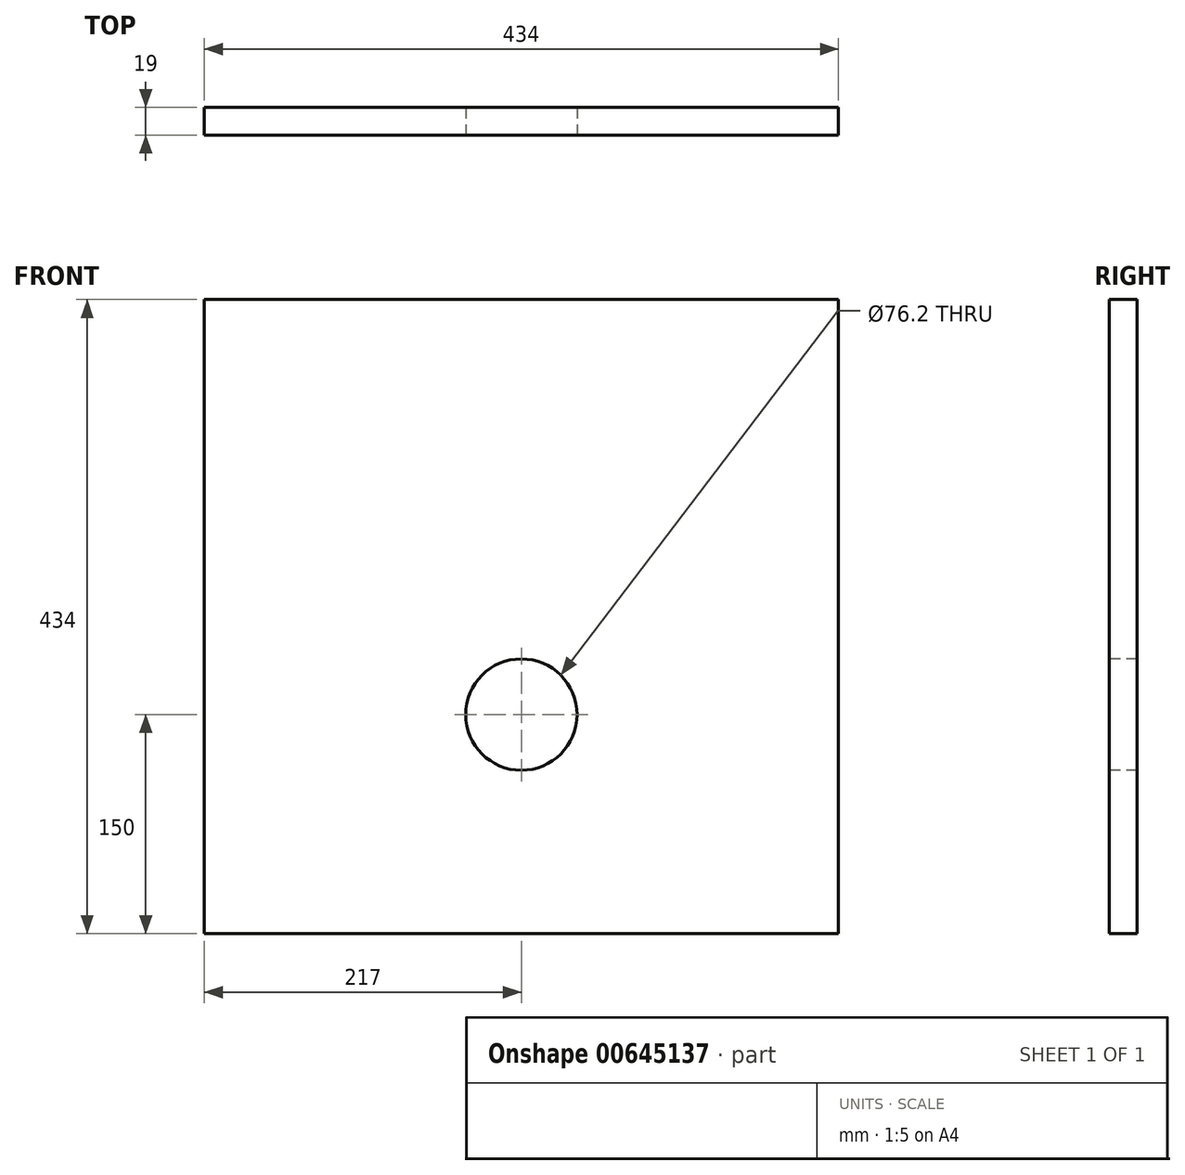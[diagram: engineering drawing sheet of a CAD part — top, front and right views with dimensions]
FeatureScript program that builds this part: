
annotation { "Feature Type Name" : "Feature", "Feature Type Description" : "" }
export const myFeature = defineFeature(function(context is Context, id is Id, definition is map)
    precondition{}
    {
        {
            var Q0;
            Q0=qCreatedBy(makeId("Front.planeOp"),FACE);
            var sketch = newSketch(context, id + "F0", { "sketchPlane" : qUnion([Q0])});
            skLineSegment(sketch, "E0.bottom", {"start": v(217, -217) * mm, "end": v(-217, -217) * mm});
            skLineSegment(sketch, "E0.top", {"start": v(217, 217) * mm, "end": v(-217, 217) * mm});
            skLineSegment(sketch, "E0.left", {"start": v(217, -217) * mm, "end": v(217, 217) * mm});
            skLineSegment(sketch, "E0.right", {"start": v(-217, -217) * mm, "end": v(-217, 217) * mm});
            skPoint(sketch, "E0.middle", {"position": v(0, 0) * mm});
            skSolve(sketch);
        }
        {
            var Q0;
            Q0=qSketchRegion(id+"F0",true);
            extrude(context, id + "F1", {"entities" : qUnion([Q0]), "depth" : 19 * mm, "offsetDistance" : 25.4 * mm});
        }
        {
            var Q0;
            Q0=makeQuery(id+"F1.opExtrude","CAP_FACE",FACE,{"disambiguationData":[OSD([sQuery(id+"F0.wireOp",EDGE,"E0.bottom"),sQuery(id+"F0.wireOp",EDGE,"E0.top"),sQuery(id+"F0.wireOp",EDGE,"E0.left"),sQuery(id+"F0.wireOp",EDGE,"E0.right")])],"isStart":false});
            var sketch = newSketch(context, id + "F2", { "sketchPlane" : qUnion([Q0])});
            skCircle(sketch, "E1", {"center": v(0, -67) * mm, "radius": 38.1 * mm});
            skSolve(sketch);
        }
        {
            var Q0;
            Q0 = qSketchRegion(id + "F2", true);
            extrude(context, id + "F3", {"entities" : qUnion([Q0]), "operationType" : NewBodyOperationType.REMOVE, "oppositeDirection" : true, "depth" : 25.4 * mm, "offsetDistance" : 25.4 * mm});
        }
    });
